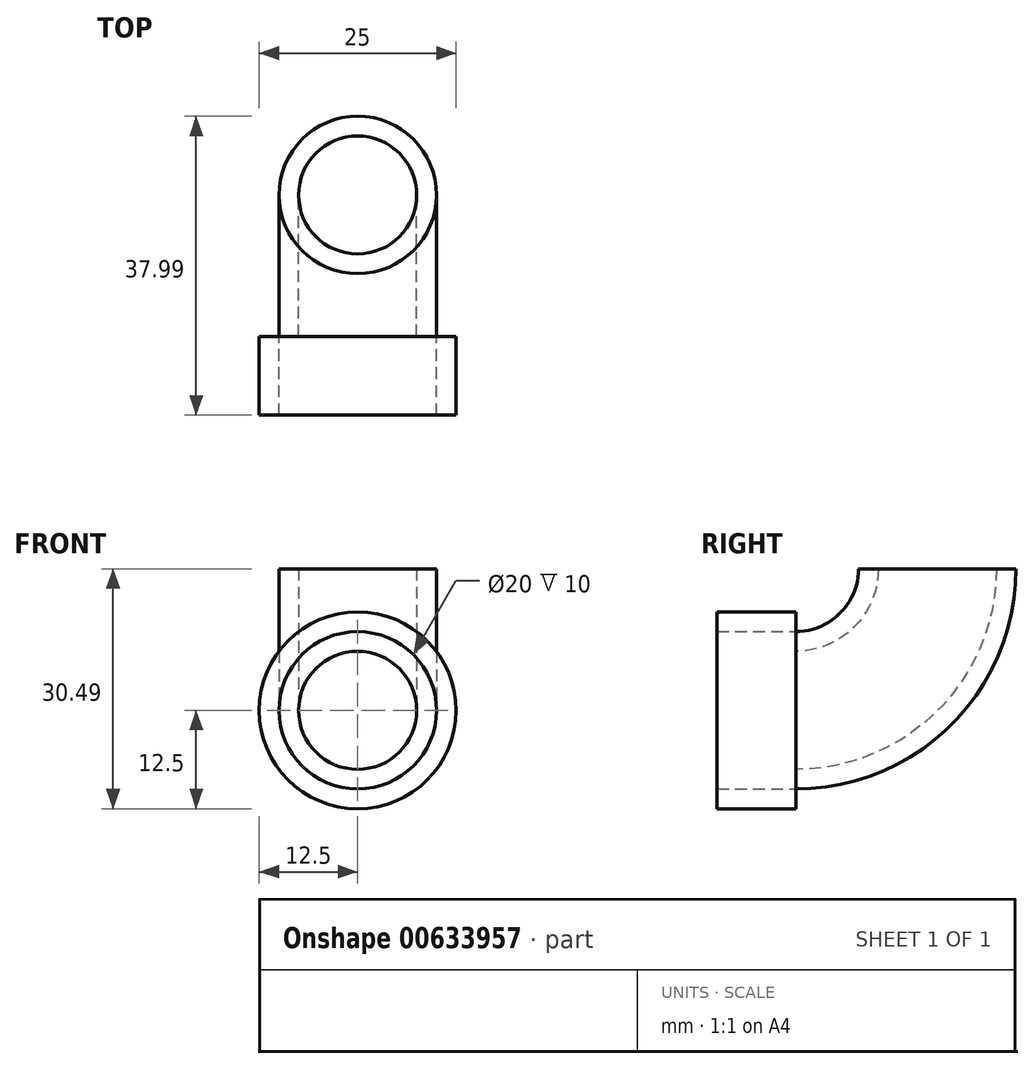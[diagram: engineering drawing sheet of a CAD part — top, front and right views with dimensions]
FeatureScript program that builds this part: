
annotation { "Feature Type Name" : "Feature", "Feature Type Description" : "" }
export const myFeature = defineFeature(function(context is Context, id is Id, definition is map)
    precondition{}
    {
        {
            var Q0;
            Q0=qCreatedBy(makeId("Front.planeOp"),FACE);
            var sketch = newSketch(context, id + "F0", { "sketchPlane" : qUnion([Q0])});
            skCircle(sketch, "E0", {"center": v(0, 0) * mm, "radius": 10 * mm});
            skCircle(sketch, "E1", {"center": v(0, 0) * mm, "radius": 7.5 * mm});
            skLineSegment(sketch, "E2", {"start": v(-12.15, 17.99) * mm, "end": v(27.51, 17.99) * mm, "construction": true});
            skSolve(sketch);
        }
        {
            var Q0;
            Q0=makeQuery(id+"F0.imprint","IMPRINT",FACE,{"disambiguationData":[TD([[makeQuery(id+"F0.imprint","IMPRINT",EDGE,{"derivedFrom":sQuery(id+"F0.wireOp",EDGE,"E0")}),1.0]])]});
            var Q1;
            Q1=sQuery(id+"F0.wireOp",EDGE,"E2");
            revolve(context, id + "F1", {"entities" : qUnion([Q0]), "axis" : qUnion([Q1]), "revolveType" : RevolveType.ONE_DIRECTION, "angle" : 90 * degree});
        }
        {
            var Q0;
            Q0=makeQuery(id+"F1.opRevolve","CAP_FACE",FACE,{"disambiguationData":[OSD([sQuery(id+"F0.wireOp",EDGE,"E0"),sQuery(id+"F0.wireOp",EDGE,"E1")])],"isStart":true});
            var sketch = newSketch(context, id + "F2", { "sketchPlane" : qUnion([Q0])});
            skCircle(sketch, "E3", {"center": v(0, 0) * mm, "radius": 12.5 * mm});
            skCircle(sketch, "E4", {"center": v(0, 0) * mm, "radius": 10 * mm});
            skSolve(sketch);
        }
        {
            var Q0;
            Q0 = qSketchRegion(id + "F2", true);
            extrude(context, id + "F3", {"entities" : qUnion([Q0]), "operationType" : NewBodyOperationType.ADD, "depth" : 10 * mm, "offsetDistance" : 25 * mm});
        }
    });
